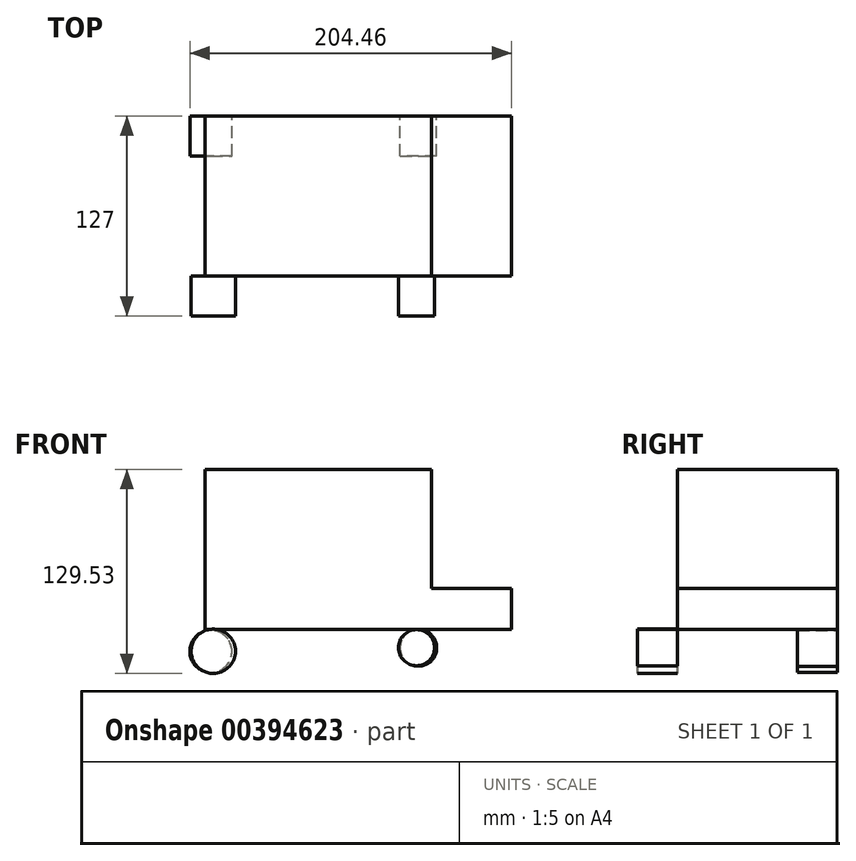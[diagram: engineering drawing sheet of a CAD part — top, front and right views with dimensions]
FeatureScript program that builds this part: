
annotation { "Feature Type Name" : "Feature", "Feature Type Description" : "" }
export const myFeature = defineFeature(function(context is Context, id is Id, definition is map)
    precondition{}
    {
        {
            var Q0;
            Q0=qCreatedBy(makeId("Front.planeOp"),FACE);
            var sketch = newSketch(context, id + "F0", { "sketchPlane" : qUnion([Q0])});
            skLineSegment(sketch, "E0.bottom", {"start": v(52.94, 37.15) * mm, "end": v(-91.05, 37.15) * mm});
            skLineSegment(sketch, "E0.top", {"start": v(52.94, -64.45) * mm, "end": v(-91.05, -64.45) * mm});
            skLineSegment(sketch, "E0.left", {"start": v(52.94, 37.15) * mm, "end": v(52.94, -64.45) * mm});
            skLineSegment(sketch, "E0.right", {"start": v(-91.05, 37.15) * mm, "end": v(-91.05, -64.45) * mm});
            skLineSegment(sketch, "E1.bottom", {"start": v(52.94, -38.49) * mm, "end": v(103.74, -38.49) * mm});
            skLineSegment(sketch, "E1.top", {"start": v(52.94, -64.46) * mm, "end": v(103.74, -64.46) * mm});
            skLineSegment(sketch, "E1.left", {"start": v(52.94, -38.49) * mm, "end": v(52.94, -64.46) * mm});
            skLineSegment(sketch, "E1.right", {"start": v(103.74, -38.49) * mm, "end": v(103.74, -64.46) * mm});
            skSolve(sketch);
        }
        {
            var Q0;
            Q0=makeQuery(id+"F0.imprint","IMPRINT",FACE,{"disambiguationData":[TD([[makeQuery(id+"F0.imprint","IMPRINT",EDGE,{"derivedFrom":sQuery(id+"F0.wireOp",EDGE,"E0.bottom")}),1.0]])]});
            var Q1;
            {var subQ3=sQuery(id+"F0.wireOp",EDGE,"E1.bottom");Q1=makeQuery(id+"F0.imprint","IMPRINT",FACE,{"disambiguationData":[TD([[makeQuery(id+"F0.imprint","IMPRINT",EDGE,{"derivedFrom":subQ3}),-1.0]])]});}
            extrude(context, id + "F1", {"entities" : qUnion([Q0, Q1]), "depth" : 101.6 * mm});
        }
        {
            var Q0;
            Q0=qCreatedBy(makeId("Front.planeOp"),FACE);
            var sketch = newSketch(context, id + "F2", { "sketchPlane" : qUnion([Q0])});
            skLineSegment(sketch, "E2.bottom", {"start": v(51.1, -5.3) * mm, "end": v(13.55, -5.3) * mm});
            skLineSegment(sketch, "E2.top", {"start": v(51.1, -37.73) * mm, "end": v(13.55, -37.73) * mm});
            skLineSegment(sketch, "E2.left", {"start": v(51.1, -5.3) * mm, "end": v(51.1, -37.73) * mm});
            skLineSegment(sketch, "E2.right", {"start": v(13.55, -5.3) * mm, "end": v(13.55, -37.73) * mm});
            skLineSegment(sketch, "E3.bottom", {"start": v(13.36, -37.54) * mm, "end": v(-31.2, -37.54) * mm});
            skLineSegment(sketch, "E3.top", {"start": v(13.36, -5.69) * mm, "end": v(-31.2, -5.69) * mm});
            skLineSegment(sketch, "E3.left", {"start": v(13.36, -37.54) * mm, "end": v(13.36, -5.69) * mm});
            skLineSegment(sketch, "E3.right", {"start": v(-31.2, -37.54) * mm, "end": v(-31.2, -5.69) * mm});
            skLineSegment(sketch, "E4.bottom", {"start": v(-35.18, -5.69) * mm, "end": v(-68.92, -5.69) * mm});
            skLineSegment(sketch, "E4.top", {"start": v(-35.18, -38.49) * mm, "end": v(-68.92, -38.49) * mm});
            skLineSegment(sketch, "E4.left", {"start": v(-35.18, -5.69) * mm, "end": v(-35.18, -38.49) * mm});
            skLineSegment(sketch, "E4.right", {"start": v(-68.92, -5.69) * mm, "end": v(-68.92, -38.49) * mm});
            skSolve(sketch);
        }
        {
            var Q0;
            Q0 = qSketchRegion(id + "F2", true);
            extrude(context, id + "F3", {"entities" : qUnion([Q0]), "operationType" : NewBodyOperationType.ADD, "depth" : 2.54 * mm});
        }
        {
            var Q0;
            Q0=makeQuery(id+"F1.opExtrude","CAP_FACE",FACE,{"disambiguationData":[OSD([sQuery(id+"F0.wireOp",EDGE,"E0.bottom"),sQuery(id+"F0.wireOp",EDGE,"E0.top"),sQuery(id+"F0.wireOp",EDGE,"E0.left"),sQuery(id+"F0.wireOp",EDGE,"E0.right"),sQuery(id+"F0.wireOp",EDGE,"E1.bottom"),sQuery(id+"F0.wireOp",EDGE,"E1.top"),sQuery(id+"F0.wireOp",EDGE,"E1.left"),sQuery(id+"F0.wireOp",EDGE,"E1.right")])],"isStart":false});
            var sketch = newSketch(context, id + "F4", { "sketchPlane" : qUnion([Q0])});
            skCircle(sketch, "E5", {"center": v(-85.8, -78.3) * mm, "radius": 14.08 * mm});
            skCircle(sketch, "E6", {"center": v(43.32, -76.03) * mm, "radius": 11.45 * mm});
            skSolve(sketch);
        }
        {
            var Q0;
            Q0 = qSketchRegion(id + "F4", true);
            extrude(context, id + "F5", {"entities" : qUnion([Q0]), "operationType" : NewBodyOperationType.ADD, "depth" : 25.4 * mm});
        }
        {
            var Q0;
            Q0=makeQuery(id+"F1.opExtrude","CAP_FACE",FACE,{"disambiguationData":[OSD([sQuery(id+"F0.wireOp",EDGE,"E0.bottom"),sQuery(id+"F0.wireOp",EDGE,"E0.top"),sQuery(id+"F0.wireOp",EDGE,"E0.left"),sQuery(id+"F0.wireOp",EDGE,"E0.right"),sQuery(id+"F0.wireOp",EDGE,"E1.bottom"),sQuery(id+"F0.wireOp",EDGE,"E1.top"),sQuery(id+"F0.wireOp",EDGE,"E1.left"),sQuery(id+"F0.wireOp",EDGE,"E1.right")])],"isStart":true});
            var sketch = newSketch(context, id + "F6", { "sketchPlane" : qUnion([Q0])});
            skCircle(sketch, "E7", {"center": v(-44.48, -76.12) * mm, "radius": 11.64 * mm});
            skCircle(sketch, "E8", {"center": v(87.34, -78.38) * mm, "radius": 13.38 * mm});
            skSolve(sketch);
        }
        {
            var Q0;
            Q0=makeQuery(id+"F6.imprint","IMPRINT",FACE,{"disambiguationData":[TD([[makeQuery(id+"F6.imprint","IMPRINT",EDGE,{"derivedFrom":sQuery(id+"F6.wireOp",EDGE,"E8")}),1.0]])]});
            var Q1;
            Q1=makeQuery(id+"F6.imprint","IMPRINT",FACE,{"disambiguationData":[TD([[makeQuery(id+"F6.imprint","IMPRINT",EDGE,{"derivedFrom":sQuery(id+"F6.wireOp",EDGE,"E7")}),1.0]])]});
            extrude(context, id + "F7", {"entities" : qUnion([Q0, Q1]), "oppositeDirection" : true, "depth" : 25.4 * mm});
        }
    });
